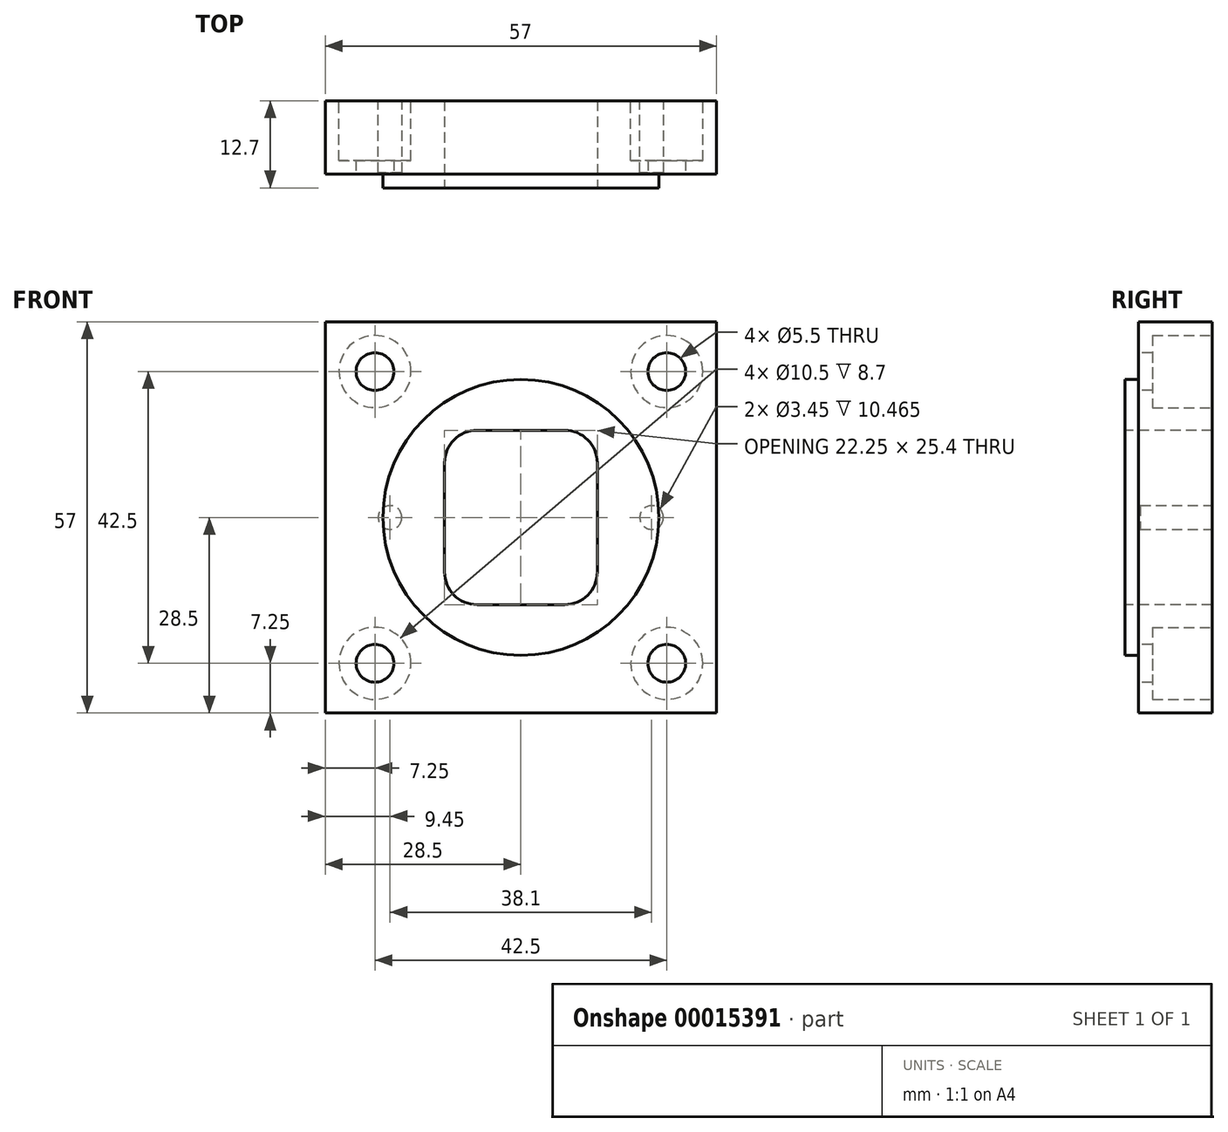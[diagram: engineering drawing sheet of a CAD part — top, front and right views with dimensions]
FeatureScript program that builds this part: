
annotation { "Feature Type Name" : "Feature", "Feature Type Description" : "" }
export const myFeature = defineFeature(function(context is Context, id is Id, definition is map)
    precondition{}
    {
        {
            var Q0;
            Q0=qCreatedBy(makeId("Front.planeOp"),FACE);
            var sketch = newSketch(context, id + "F0", { "sketchPlane" : qUnion([Q0])});
            skLineSegment(sketch, "E0.rect.bottom", {"start": v(-28.5, 28.5) * mm, "end": v(28.5, 28.5) * mm});
            skLineSegment(sketch, "E0.rect.top", {"start": v(-28.5, -28.5) * mm, "end": v(28.5, -28.5) * mm});
            skLineSegment(sketch, "E0.rect.left", {"start": v(-28.5, 28.5) * mm, "end": v(-28.5, -28.5) * mm});
            skLineSegment(sketch, "E0.rect.right", {"start": v(28.5, 28.5) * mm, "end": v(28.5, -28.5) * mm});
            skPoint(sketch, "E0.rect.middle", {"position": v(0, 0) * mm});
            skSolve(sketch);
        }
        {
            var Q0;
            Q0 = qSketchRegion(id + "F0", true);
            extrude(context, id + "F1", {"entities" : qUnion([Q0]), "depth" : 12.7 * mm});
        }
        {
            var Q0;
            Q0=makeQuery(id+"F1.opExtrude","CAP_FACE",FACE,{"disambiguationData":[OSD([sQuery(id+"F0.wireOp",EDGE,"E0.rect.bottom"),sQuery(id+"F0.wireOp",EDGE,"E0.rect.top"),sQuery(id+"F0.wireOp",EDGE,"E0.rect.left"),sQuery(id+"F0.wireOp",EDGE,"E0.rect.right")])],"isStart":false});
            var sketch = newSketch(context, id + "F2", { "sketchPlane" : qUnion([Q0])});
            skLineSegment(sketch, "E1.rect.bottom", {"start": v(11.12, 12.7) * mm, "end": v(-11.12, 12.7) * mm});
            skLineSegment(sketch, "E1.rect.top", {"start": v(11.13, -12.7) * mm, "end": v(-11.12, -12.7) * mm});
            skLineSegment(sketch, "E1.rect.left", {"start": v(11.12, 12.7) * mm, "end": v(11.13, -12.7) * mm});
            skLineSegment(sketch, "E1.rect.right", {"start": v(-11.12, 12.7) * mm, "end": v(-11.12, -12.7) * mm});
            skPoint(sketch, "E1.rect.middle", {"position": v(0, 0) * mm});
            skLineSegment(sketch, "E2", {"start": v(-28.5, 0) * mm, "end": v(28.5, 0) * mm, "construction": true});
            skSolve(sketch);
        }
        {
            var Q0;
            Q0 = qSketchRegion(id + "F2", true);
            extrude(context, id + "F3", {"entities" : qUnion([Q0]), "operationType" : NewBodyOperationType.REMOVE, "endBound" : BoundingType.THROUGH_ALL, "oppositeDirection" : true, "depth" : 25.4 * mm});
        }
        {
            var Q0;
            Q0=makeQuery(id+"F1.opExtrude","CAP_FACE",FACE,{"disambiguationData":[OSD([sQuery(id+"F0.wireOp",EDGE,"E0.rect.bottom"),sQuery(id+"F0.wireOp",EDGE,"E0.rect.top"),sQuery(id+"F0.wireOp",EDGE,"E0.rect.left"),sQuery(id+"F0.wireOp",EDGE,"E0.rect.right")])],"isStart":false});
            var sketch = newSketch(context, id + "F4", { "sketchPlane" : qUnion([Q0])});
            skCircle(sketch, "E3", {"center": v(0, 0) * mm, "radius": 20.1 * mm});
            skLineSegment(sketch, "E4.bottom", {"start": v(-28.5, 28.5) * mm, "end": v(28.5, 28.5) * mm});
            skLineSegment(sketch, "E4.top", {"start": v(-28.5, -28.5) * mm, "end": v(28.5, -28.5) * mm});
            skLineSegment(sketch, "E4.left", {"start": v(-28.5, 28.5) * mm, "end": v(-28.5, -28.5) * mm});
            skLineSegment(sketch, "E4.right", {"start": v(28.5, 28.5) * mm, "end": v(28.5, -28.5) * mm});
            skSolve(sketch);
        }
        {
            var Q0;
            Q0 = qSketchRegion(id + "F4", true);
            extrude(context, id + "F5", {"entities" : qUnion([Q0]), "operationType" : NewBodyOperationType.REMOVE, "oppositeDirection" : true, "depth" : 2 * mm});
        }
        {
            var Q0;
            Q0=makeQuery(id+"F1.opExtrude","CAP_FACE",FACE,{"disambiguationData":[OSD([sQuery(id+"F0.wireOp",EDGE,"E0.rect.bottom"),sQuery(id+"F0.wireOp",EDGE,"E0.rect.top"),sQuery(id+"F0.wireOp",EDGE,"E0.rect.left"),sQuery(id+"F0.wireOp",EDGE,"E0.rect.right")])],"isStart":true});
            var sketch = newSketch(context, id + "F6", { "sketchPlane" : qUnion([Q0])});
            skCircle(sketch, "E5", {"center": v(19.05, 0) * mm, "radius": 1.73 * mm});
            skCircle(sketch, "E6", {"center": v(-19.05, 0) * mm, "radius": 1.73 * mm});
            skSolve(sketch);
        }
        {
            var Q0;
            Q0 = qSketchRegion(id + "F6", true);
            extrude(context, id + "F7", {"entities" : qUnion([Q0]), "operationType" : NewBodyOperationType.REMOVE, "oppositeDirection" : true, "depth" : 10.46 * mm});
        }
        {
            var Q0;
            Q0=makeQuery(id+"F5.boolean.opBoolean","COPY",FACE,{"derivedFrom":makeQuery(id+"F5.opExtrude","CAP_FACE",FACE,{"disambiguationData":[OSD([sQuery(id+"F4.wireOp",EDGE,"E3"),sQuery(id+"F4.wireOp",EDGE,"E4.bottom"),sQuery(id+"F4.wireOp",EDGE,"E4.top"),sQuery(id+"F4.wireOp",EDGE,"E4.left"),sQuery(id+"F4.wireOp",EDGE,"E4.right")])],"isStart":false})});
            var sketch = newSketch(context, id + "F8", { "sketchPlane" : qUnion([Q0])});
            skLineSegment(sketch, "E7.bottom", {"start": v(21.25, -21.25) * mm, "end": v(-21.25, -21.25) * mm, "construction": true});
            skLineSegment(sketch, "E7.top", {"start": v(21.25, 21.25) * mm, "end": v(-21.25, 21.25) * mm, "construction": true});
            skLineSegment(sketch, "E7.left", {"start": v(21.25, -21.25) * mm, "end": v(21.25, 21.25) * mm, "construction": true});
            skLineSegment(sketch, "E7.right", {"start": v(-21.25, -21.25) * mm, "end": v(-21.25, 21.25) * mm, "construction": true});
            skCircle(sketch, "E8", {"center": v(21.25, -21.25) * mm, "radius": 2.75 * mm});
            skCircle(sketch, "E9", {"center": v(-21.25, -21.25) * mm, "radius": 2.75 * mm});
            skCircle(sketch, "E10", {"center": v(-21.25, 21.25) * mm, "radius": 2.75 * mm});
            skCircle(sketch, "E11", {"center": v(21.25, 21.25) * mm, "radius": 2.75 * mm});
            skSolve(sketch);
        }
        {
            var Q0;
            Q0 = qSketchRegion(id + "F8", true);
            extrude(context, id + "F9", {"entities" : qUnion([Q0]), "operationType" : NewBodyOperationType.REMOVE, "endBound" : BoundingType.THROUGH_ALL, "oppositeDirection" : true, "depth" : 25.4 * mm});
        }
        {
            var Q0;
            Q0=makeQuery(id+"F1.opExtrude","CAP_FACE",FACE,{"disambiguationData":[OSD([sQuery(id+"F0.wireOp",EDGE,"E0.rect.bottom"),sQuery(id+"F0.wireOp",EDGE,"E0.rect.top"),sQuery(id+"F0.wireOp",EDGE,"E0.rect.left"),sQuery(id+"F0.wireOp",EDGE,"E0.rect.right")])],"isStart":true});
            var sketch = newSketch(context, id + "F10", { "sketchPlane" : qUnion([Q0])});
            skCircle(sketch, "E12", {"center": v(-21.25, 21.25) * mm, "radius": 5.25 * mm});
            skCircle(sketch, "E13", {"center": v(21.25, 21.25) * mm, "radius": 5.25 * mm});
            skCircle(sketch, "E14", {"center": v(21.25, -21.25) * mm, "radius": 5.25 * mm});
            skCircle(sketch, "E15", {"center": v(-21.25, -21.25) * mm, "radius": 5.25 * mm});
            skSolve(sketch);
        }
        {
            var Q0;
            Q0 = qSketchRegion(id + "F10", true);
            extrude(context, id + "F11", {"entities" : qUnion([Q0]), "operationType" : NewBodyOperationType.REMOVE, "oppositeDirection" : true, "depth" : 8.7 * mm});
        }
        {
            var Q0;
            Q0=makeQuery(id+"F3.boolean.opBoolean","COPY",EDGE,{"derivedFrom":makeQuery(id+"F3.opExtrude","SWEPT_EDGE",EDGE,{"disambiguationData":[OSD([sQuery(id+"F2.wireOp",EDGE,"E1.rect.top"),sQuery(id+"F2.wireOp",EDGE,"E1.rect.left")])]})});
            var Q1;
            Q1=makeQuery(id+"F3.boolean.opBoolean","COPY",EDGE,{"derivedFrom":makeQuery(id+"F3.opExtrude","SWEPT_EDGE",EDGE,{"disambiguationData":[OSD([sQuery(id+"F2.wireOp",EDGE,"E1.rect.top"),sQuery(id+"F2.wireOp",EDGE,"E1.rect.right")])]})});
            var Q2;
            Q2=makeQuery(id+"F3.boolean.opBoolean","COPY",EDGE,{"derivedFrom":makeQuery(id+"F3.opExtrude","SWEPT_EDGE",EDGE,{"disambiguationData":[OSD([sQuery(id+"F2.wireOp",EDGE,"E1.rect.bottom"),sQuery(id+"F2.wireOp",EDGE,"E1.rect.right")])]})});
            var Q3;
            Q3=makeQuery(id+"F3.boolean.opBoolean","COPY",EDGE,{"derivedFrom":makeQuery(id+"F3.opExtrude","SWEPT_EDGE",EDGE,{"disambiguationData":[OSD([sQuery(id+"F2.wireOp",EDGE,"E1.rect.bottom"),sQuery(id+"F2.wireOp",EDGE,"E1.rect.left")])]})});
            fillet(context, id + "F12", {"entities" : qUnion([Q0, Q1, Q2, Q3]), "radius" : 4.75 * mm, "tangentPropagation" : true, "allowEdgeOverflow" : false});
        }
    });
